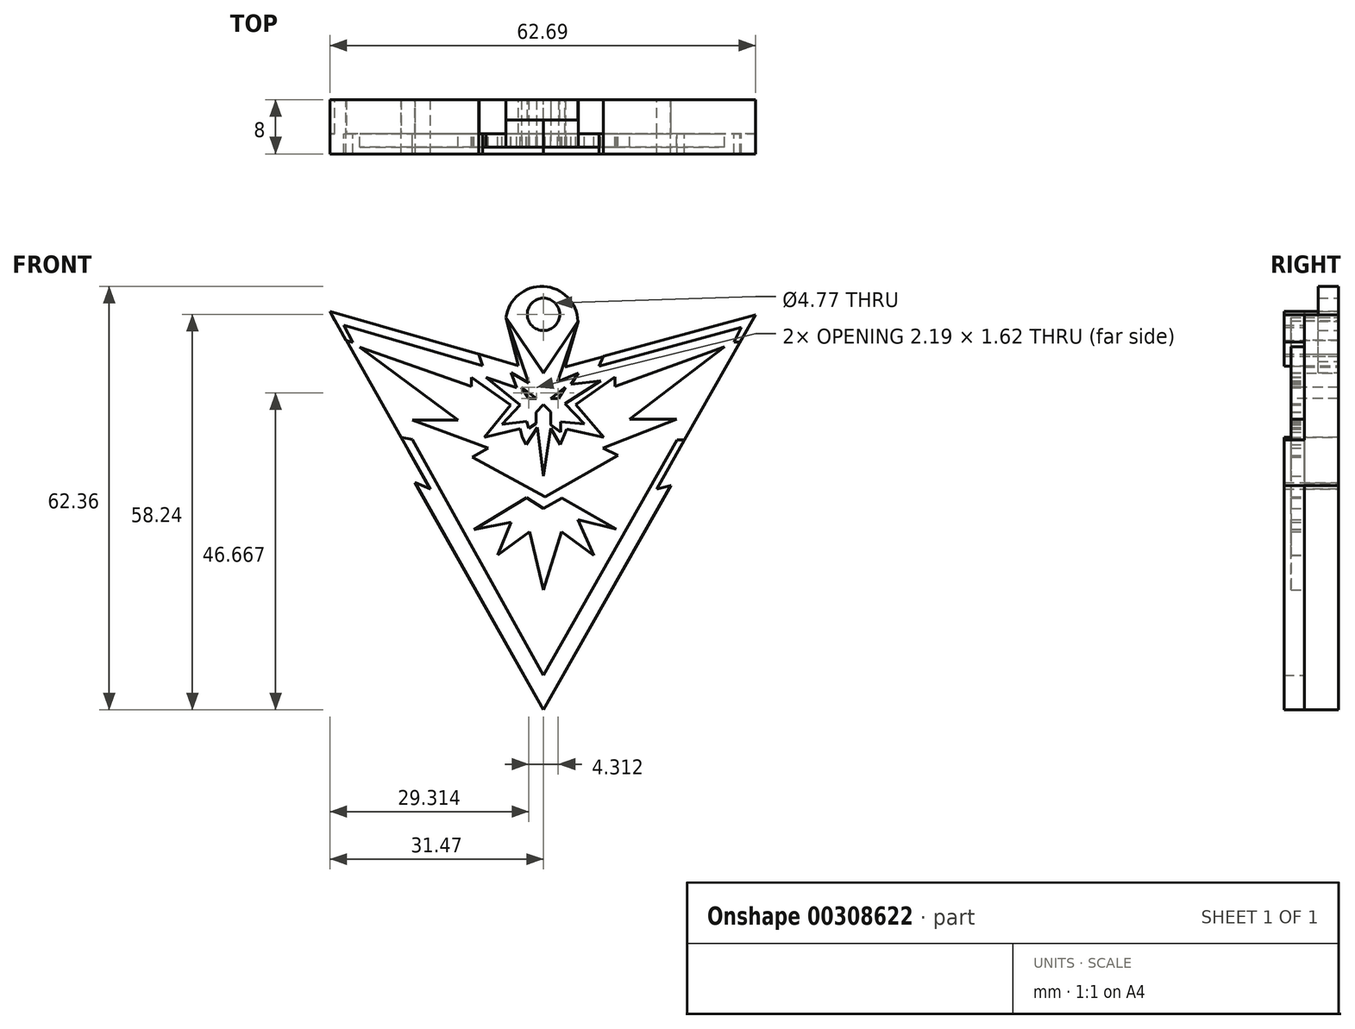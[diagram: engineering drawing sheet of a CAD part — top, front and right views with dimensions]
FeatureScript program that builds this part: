
annotation { "Feature Type Name" : "Feature", "Feature Type Description" : "" }
export const myFeature = defineFeature(function(context is Context, id is Id, definition is map)
    precondition{}
    {
        {
            var Q0;
            Q0=qCreatedBy(makeId("Front.planeOp"),FACE);
            var sketch = newSketch(context, id + "F0", { "sketchPlane" : qUnion([Q0])});
            skLineSegment(sketch, "E0", {"start": v(-31.47, 27.97) * mm, "end": v(-16.64, 1.77) * mm});
            skLineSegment(sketch, "E1", {"start": v(-16.64, 1.77) * mm, "end": v(-18.92, 2.74) * mm});
            skLineSegment(sketch, "E2", {"start": v(-18.92, 2.74) * mm, "end": v(0, -30.7) * mm});
            skLineSegment(sketch, "E3", {"start": v(0, -30.7) * mm, "end": v(18.75, 2.34) * mm});
            skLineSegment(sketch, "E4", {"start": v(18.75, 2.34) * mm, "end": v(16.66, 1.81) * mm});
            skLineSegment(sketch, "E5", {"start": v(16.66, 1.81) * mm, "end": v(31.22, 27.46) * mm});
            skLineSegment(sketch, "E6", {"start": v(31.22, 27.46) * mm, "end": v(3.16, 19.8) * mm});
            skLineSegment(sketch, "E7", {"start": v(-9.51, 21.66) * mm, "end": v(-31.47, 27.97) * mm});
            skPoint(sketch, "E8.start.orphan", {"position": v(0, 17.27) * mm});
            skPoint(sketch, "E9.start.orphan", {"position": v(0, -25.6) * mm});
            skLineSegment(sketch, "E10", {"start": v(-29.08, 23.73) * mm, "end": v(-28.03, 23.44) * mm});
            skLineSegment(sketch, "E11", {"start": v(-28.03, 23.44) * mm, "end": v(-29.42, 25.88) * mm});
            skLineSegment(sketch, "E12", {"start": v(-29.42, 25.88) * mm, "end": v(-8.9, 19.99) * mm});
            skLineSegment(sketch, "E13", {"start": v(-8.9, 19.99) * mm, "end": v(-9.51, 21.66) * mm});
            skLineSegment(sketch, "E14", {"start": v(-20.99, 9.44) * mm, "end": v(-19.31, 9.1) * mm});
            skLineSegment(sketch, "E15", {"start": v(-19.31, 9.1) * mm, "end": v(0, -25.6) * mm});
            skLineSegment(sketch, "E16", {"start": v(0, -25.6) * mm, "end": v(19.67, 9.04) * mm});
            skLineSegment(sketch, "E17", {"start": v(19.67, 9.04) * mm, "end": v(20.77, 9.04) * mm});
            skLineSegment(sketch, "E18", {"start": v(8.86, 21.35) * mm, "end": v(8.22, 19.92) * mm});
            skLineSegment(sketch, "E19", {"start": v(8.22, 19.92) * mm, "end": v(29.1, 25.63) * mm});
            skLineSegment(sketch, "E20", {"start": v(29.1, 25.63) * mm, "end": v(28.09, 23.5) * mm});
            skLineSegment(sketch, "E21", {"start": v(28.09, 23.5) * mm, "end": v(28.97, 23.5) * mm});
            skLineSegment(sketch, "E22", {"start": v(-9.51, 21.66) * mm, "end": v(-3.7, 19.99) * mm});
            skLineSegment(sketch, "E23", {"start": v(-3.7, 19.99) * mm, "end": v(-5.57, 27.1) * mm});
            skLineSegment(sketch, "E24", {"start": v(-5.57, 27.1) * mm, "end": v(0, 18.93) * mm});
            skLineSegment(sketch, "E25", {"start": v(0, 18.93) * mm, "end": v(5.11, 26.6) * mm});
            skLineSegment(sketch, "E26", {"start": v(5.11, 26.6) * mm, "end": v(3.16, 19.8) * mm});
            skSolve(sketch);
        }
        {
            var Q0;
            {var subQ1=sQuery(id+"F0.wireOp",EDGE,"E7");Q0=makeQuery(id+"F0.imprint","IMPRINT",FACE,{"disambiguationData":[TD([[makeQuery(id+"F0.imprint","IMPRINT",EDGE,{"derivedFrom":subQ1}),1.0]])]});}
            var Q1;
            {var subQ1=sQuery(id+"F0.wireOp",EDGE,"E10");Q1=makeQuery(id+"F0.imprint","IMPRINT",FACE,{"disambiguationData":[TD([[makeQuery(id+"F0.imprint","IMPRINT",EDGE,{"derivedFrom":subQ1}),-1.0]])]});}
            var Q2;
            {var subQ0=sQuery(id+"F0.wireOp",EDGE,"E18");Q2=makeQuery(id+"F0.imprint","IMPRINT",FACE,{"disambiguationData":[TD([[makeQuery(id+"F0.imprint","IMPRINT",EDGE,{"derivedFrom":subQ0}),1.0]])]});}
            var Q3;
            {var subQ0=sQuery(id+"F0.wireOp",EDGE,"E1");Q3=makeQuery(id+"F0.imprint","IMPRINT",FACE,{"disambiguationData":[TD([[makeQuery(id+"F0.imprint","IMPRINT",EDGE,{"derivedFrom":subQ0}),1.0]])]});}
            extrude(context, id + "F1", {"entities" : qUnion([Q0, Q1, Q2, Q3]), "depth" : 5 * mm, "offsetDistance" : 25 * mm});
        }
        {
            var Q0;
            Q0=qCreatedBy(makeId("Front.planeOp"),FACE);
            var sketch = newSketch(context, id + "F2", { "sketchPlane" : qUnion([Q0])});
            skLineSegment(sketch, "E27", {"start": v(-31.46, 27.99) * mm, "end": v(-29.13, 23.73) * mm});
            skLineSegment(sketch, "E28", {"start": v(-29.13, 23.73) * mm, "end": v(-28.06, 23.43) * mm});
            skLineSegment(sketch, "E29", {"start": v(-28.06, 23.43) * mm, "end": v(-29.43, 25.93) * mm});
            skLineSegment(sketch, "E30", {"start": v(-29.43, 25.93) * mm, "end": v(-8.95, 20) * mm});
            skLineSegment(sketch, "E31", {"start": v(-8.95, 20) * mm, "end": v(-9.52, 21.7) * mm});
            skLineSegment(sketch, "E32", {"start": v(-9.52, 21.7) * mm, "end": v(-31.46, 27.99) * mm});
            skLineSegment(sketch, "E33", {"start": v(8.82, 21.38) * mm, "end": v(8.17, 19.92) * mm});
            skLineSegment(sketch, "E34", {"start": v(8.17, 19.92) * mm, "end": v(29.15, 25.63) * mm});
            skLineSegment(sketch, "E35", {"start": v(29.15, 25.63) * mm, "end": v(28.06, 23.5) * mm});
            skLineSegment(sketch, "E36", {"start": v(28.06, 23.5) * mm, "end": v(28.95, 23.5) * mm});
            skLineSegment(sketch, "E37", {"start": v(28.95, 23.5) * mm, "end": v(31.2, 27.48) * mm});
            skLineSegment(sketch, "E38", {"start": v(31.2, 27.48) * mm, "end": v(8.82, 21.38) * mm});
            skLineSegment(sketch, "E39", {"start": v(-21, 9.43) * mm, "end": v(-19.32, 9.1) * mm});
            skLineSegment(sketch, "E40", {"start": v(-19.32, 9.1) * mm, "end": v(0, -25.6) * mm});
            skLineSegment(sketch, "E41", {"start": v(0, -25.6) * mm, "end": v(19.66, 9.05) * mm});
            skLineSegment(sketch, "E42", {"start": v(19.66, 9.05) * mm, "end": v(20.77, 9.05) * mm});
            skLineSegment(sketch, "E43", {"start": v(20.77, 9.05) * mm, "end": v(16.68, 1.83) * mm});
            skLineSegment(sketch, "E44", {"start": v(16.68, 1.83) * mm, "end": v(18.74, 2.36) * mm});
            skLineSegment(sketch, "E45", {"start": v(18.74, 2.36) * mm, "end": v(0, -30.67) * mm});
            skLineSegment(sketch, "E46", {"start": v(0, -30.67) * mm, "end": v(-18.9, 2.77) * mm});
            skLineSegment(sketch, "E47", {"start": v(-18.9, 2.77) * mm, "end": v(-16.64, 1.83) * mm});
            skLineSegment(sketch, "E48", {"start": v(-16.64, 1.83) * mm, "end": v(-21, 9.43) * mm});
            skSolve(sketch);
        }
        {
            var Q0;
            Q0 = qSketchRegion(id + "F2", true);
            extrude(context, id + "F3", {"entities" : qUnion([Q0]), "operationType" : NewBodyOperationType.ADD, "depth" : 8 * mm, "offsetDistance" : 25 * mm});
        }
        {
            var Q0;
            {var subQ0=sQuery(id+"F0.wireOp",EDGE,"E6");var subQ1=sQuery(id+"F0.wireOp",EDGE,"E5");var subQ2=sQuery(id+"F0.wireOp",EDGE,"E26");var subQ3=sQuery(id+"F0.wireOp",EDGE,"E25");var subQ4=sQuery(id+"F0.wireOp",EDGE,"E23");var subQ5=sQuery(id+"F0.wireOp",EDGE,"E24");var subQ6=sQuery(id+"F0.wireOp",EDGE,"E0");var subQ7=sQuery(id+"F0.wireOp",EDGE,"E22");var subQ8=sQuery(id+"F0.wireOp",EDGE,"E7");Q0=makeQuery(id+"F3.boolean.opBoolean","SPLIT",FACE,{"disambiguationData":[TD([makeQuery(id+"F1.opExtrude","SWEPT_FACE",FACE,{"disambiguationData":[OSD([subQ1])]})])],"derivedFrom":makeQuery(id+"F1.opExtrude","CAP_FACE",FACE,{"disambiguationData":[OSD([subQ6,sQuery(id+"F0.wireOp",EDGE,"E1"),sQuery(id+"F0.wireOp",EDGE,"E2"),sQuery(id+"F0.wireOp",EDGE,"E3"),sQuery(id+"F0.wireOp",EDGE,"E4"),subQ1,subQ0,subQ8,subQ7,subQ4,subQ5,subQ3,subQ2])],"isStart":false})});}
            var sketch = newSketch(context, id + "F4", { "sketchPlane" : qUnion([Q0])});
            skLineSegment(sketch, "E49", {"start": v(-10.21, -4.18) * mm, "end": v(-2.48, 0.56) * mm});
            skLineSegment(sketch, "E50", {"start": v(-2.48, 0.56) * mm, "end": v(0, -1.04) * mm});
            skLineSegment(sketch, "E51", {"start": v(0, -1.04) * mm, "end": v(2.74, 0.47) * mm});
            skLineSegment(sketch, "E52", {"start": v(2.74, 0.47) * mm, "end": v(10.73, -4.09) * mm});
            skLineSegment(sketch, "E53", {"start": v(10.73, -4.09) * mm, "end": v(5.05, -2.7) * mm});
            skLineSegment(sketch, "E54", {"start": v(5.05, -2.7) * mm, "end": v(7.42, -7.93) * mm});
            skLineSegment(sketch, "E55", {"start": v(7.42, -7.93) * mm, "end": v(2.68, -4.44) * mm});
            skLineSegment(sketch, "E56", {"start": v(2.68, -4.44) * mm, "end": v(0, -13.06) * mm});
            skLineSegment(sketch, "E57", {"start": v(0, -13.06) * mm, "end": v(-2.07, -4.47) * mm});
            skLineSegment(sketch, "E58", {"start": v(-2.07, -4.47) * mm, "end": v(-6.78, -7.87) * mm});
            skLineSegment(sketch, "E59", {"start": v(-6.78, -7.87) * mm, "end": v(-4.8, -3.1) * mm});
            skLineSegment(sketch, "E60", {"start": v(-4.8, -3.1) * mm, "end": v(-10.21, -4.18) * mm});
            skSolve(sketch);
        }
        {
            var Q0;
            Q0 = qSketchRegion(id + "F4", true);
            extrude(context, id + "F5", {"entities" : qUnion([Q0]), "operationType" : NewBodyOperationType.ADD, "depth" : 2 * mm});
        }
        {
            var Q0;
            {var subQ0=sQuery(id+"F0.wireOp",EDGE,"E6");var subQ1=sQuery(id+"F0.wireOp",EDGE,"E5");var subQ2=sQuery(id+"F0.wireOp",EDGE,"E26");var subQ3=sQuery(id+"F0.wireOp",EDGE,"E25");var subQ4=sQuery(id+"F0.wireOp",EDGE,"E23");var subQ5=sQuery(id+"F0.wireOp",EDGE,"E24");var subQ6=sQuery(id+"F0.wireOp",EDGE,"E0");var subQ7=sQuery(id+"F0.wireOp",EDGE,"E22");var subQ8=sQuery(id+"F0.wireOp",EDGE,"E7");Q0=makeQuery(id+"F3.boolean.opBoolean","SPLIT",FACE,{"disambiguationData":[TD([makeQuery(id+"F1.opExtrude","SWEPT_FACE",FACE,{"disambiguationData":[OSD([subQ1])]})])],"derivedFrom":makeQuery(id+"F1.opExtrude","CAP_FACE",FACE,{"disambiguationData":[OSD([subQ6,sQuery(id+"F0.wireOp",EDGE,"E1"),sQuery(id+"F0.wireOp",EDGE,"E2"),sQuery(id+"F0.wireOp",EDGE,"E3"),sQuery(id+"F0.wireOp",EDGE,"E4"),subQ1,subQ0,subQ8,subQ7,subQ4,subQ5,subQ3,subQ2])],"isStart":false})});}
            var sketch = newSketch(context, id + "F6", { "sketchPlane" : qUnion([Q0])});
            skLineSegment(sketch, "E61", {"start": v(-27.04, 22.7) * mm, "end": v(-10.64, 16.92) * mm});
            skLineSegment(sketch, "E62", {"start": v(-10.64, 16.92) * mm, "end": v(-10.64, 18.24) * mm});
            skLineSegment(sketch, "E63", {"start": v(-10.64, 18.24) * mm, "end": v(-4.87, 14.18) * mm});
            skLineSegment(sketch, "E64", {"start": v(-4.87, 14.18) * mm, "end": v(-8.7, 9.43) * mm});
            skLineSegment(sketch, "E65", {"start": v(-8.7, 9.43) * mm, "end": v(-3.44, 10.7) * mm});
            skLineSegment(sketch, "E66", {"start": v(-3.44, 10.7) * mm, "end": v(-3.14, 9.43) * mm});
            skLineSegment(sketch, "E67", {"start": v(-3.14, 9.43) * mm, "end": v(-2.53, 8.35) * mm});
            skLineSegment(sketch, "E68", {"start": v(-2.53, 8.35) * mm, "end": v(-0.93, 10.87) * mm});
            skLineSegment(sketch, "E69", {"start": v(-0.93, 10.87) * mm, "end": v(0, 3.73) * mm});
            skLineSegment(sketch, "E70", {"start": v(0, 3.73) * mm, "end": v(1.07, 10.75) * mm});
            skLineSegment(sketch, "E71", {"start": v(1.07, 10.75) * mm, "end": v(2.44, 8.33) * mm});
            skLineSegment(sketch, "E72", {"start": v(2.44, 8.33) * mm, "end": v(3.41, 10.64) * mm});
            skLineSegment(sketch, "E73", {"start": v(3.41, 10.64) * mm, "end": v(8.9, 9.43) * mm});
            skLineSegment(sketch, "E74", {"start": v(8.9, 9.43) * mm, "end": v(4.73, 14.24) * mm});
            skLineSegment(sketch, "E75", {"start": v(4.73, 14.24) * mm, "end": v(10.55, 18.35) * mm});
            skLineSegment(sketch, "E76", {"start": v(10.55, 18.35) * mm, "end": v(10.55, 16.92) * mm});
            skLineSegment(sketch, "E77", {"start": v(10.55, 16.92) * mm, "end": v(26.67, 22.75) * mm});
            skLineSegment(sketch, "E78", {"start": v(26.67, 22.75) * mm, "end": v(12.67, 12.12) * mm});
            skLineSegment(sketch, "E79", {"start": v(12.67, 12.12) * mm, "end": v(19.58, 12.12) * mm});
            skLineSegment(sketch, "E80", {"start": v(19.58, 12.12) * mm, "end": v(8.73, 7.84) * mm});
            skLineSegment(sketch, "E81", {"start": v(8.73, 7.84) * mm, "end": v(10.95, 6.75) * mm});
            skLineSegment(sketch, "E82", {"start": v(10.95, 6.75) * mm, "end": v(0.24, 0.7) * mm});
            skLineSegment(sketch, "E83", {"start": v(0.24, 0.7) * mm, "end": v(-10.47, 6.53) * mm});
            skLineSegment(sketch, "E84", {"start": v(-10.47, 6.53) * mm, "end": v(-8.15, 7.84) * mm});
            skLineSegment(sketch, "E85", {"start": v(-8.15, 7.84) * mm, "end": v(-19.33, 11.95) * mm});
            skLineSegment(sketch, "E86", {"start": v(-19.33, 11.95) * mm, "end": v(-12.59, 11.95) * mm});
            skLineSegment(sketch, "E87", {"start": v(-12.59, 11.95) * mm, "end": v(-27.04, 22.7) * mm});
            skSolve(sketch);
        }
        {
            var Q0;
            Q0 = qSketchRegion(id + "F6", true);
            extrude(context, id + "F7", {"entities" : qUnion([Q0]), "operationType" : NewBodyOperationType.ADD, "depth" : 2 * mm});
        }
        {
            var Q0;
            {var subQ0=sQuery(id+"F0.wireOp",EDGE,"E6");var subQ1=sQuery(id+"F0.wireOp",EDGE,"E5");var subQ2=sQuery(id+"F0.wireOp",EDGE,"E26");var subQ3=sQuery(id+"F0.wireOp",EDGE,"E25");var subQ4=sQuery(id+"F0.wireOp",EDGE,"E23");var subQ5=sQuery(id+"F0.wireOp",EDGE,"E24");var subQ6=sQuery(id+"F0.wireOp",EDGE,"E0");var subQ7=sQuery(id+"F0.wireOp",EDGE,"E22");var subQ8=sQuery(id+"F0.wireOp",EDGE,"E7");Q0=makeQuery(id+"F3.boolean.opBoolean","SPLIT",FACE,{"disambiguationData":[TD([makeQuery(id+"F1.opExtrude","SWEPT_FACE",FACE,{"disambiguationData":[OSD([subQ1])]})])],"derivedFrom":makeQuery(id+"F1.opExtrude","CAP_FACE",FACE,{"disambiguationData":[OSD([subQ6,sQuery(id+"F0.wireOp",EDGE,"E1"),sQuery(id+"F0.wireOp",EDGE,"E2"),sQuery(id+"F0.wireOp",EDGE,"E3"),sQuery(id+"F0.wireOp",EDGE,"E4"),subQ1,subQ0,subQ8,subQ7,subQ4,subQ5,subQ3,subQ2])],"isStart":false})});}
            var sketch = newSketch(context, id + "F8", { "sketchPlane" : qUnion([Q0])});
            skLineSegment(sketch, "E88", {"start": v(-6.12, 11.34) * mm, "end": v(-3.42, 14.18) * mm});
            skLineSegment(sketch, "E89", {"start": v(-3.42, 14.18) * mm, "end": v(-8.46, 18.25) * mm});
            skLineSegment(sketch, "E90", {"start": v(-8.46, 18.25) * mm, "end": v(-3.96, 16.74) * mm});
            skLineSegment(sketch, "E91", {"start": v(-3.96, 16.74) * mm, "end": v(-4.79, 18.94) * mm});
            skLineSegment(sketch, "E92", {"start": v(-4.79, 18.94) * mm, "end": v(-2.2, 17.46) * mm});
            skLineSegment(sketch, "E93", {"start": v(-2.2, 17.46) * mm, "end": v(-5.57, 27.1) * mm});
            skLineSegment(sketch, "E94", {"start": v(-5.57, 27.1) * mm, "end": v(0, 18.93) * mm});
            skLineSegment(sketch, "E95", {"start": v(0, 18.93) * mm, "end": v(5.11, 26.6) * mm});
            skLineSegment(sketch, "E96", {"start": v(5.11, 26.6) * mm, "end": v(2.08, 17.64) * mm});
            skLineSegment(sketch, "E97", {"start": v(2.08, 17.64) * mm, "end": v(5.11, 18.93) * mm});
            skLineSegment(sketch, "E98", {"start": v(5.11, 18.93) * mm, "end": v(4.06, 17.24) * mm});
            skLineSegment(sketch, "E99", {"start": v(4.06, 17.24) * mm, "end": v(8.42, 17.75) * mm});
            skLineSegment(sketch, "E100", {"start": v(8.42, 17.75) * mm, "end": v(3.16, 14.36) * mm});
            skLineSegment(sketch, "E101", {"start": v(3.16, 14.36) * mm, "end": v(6, 11.41) * mm});
            skLineSegment(sketch, "E102", {"start": v(6, 11.41) * mm, "end": v(2.52, 11.7) * mm});
            skLineSegment(sketch, "E103", {"start": v(2.52, 11.7) * mm, "end": v(2.52, 10.23) * mm});
            skLineSegment(sketch, "E104", {"start": v(2.52, 10.23) * mm, "end": v(1.07, 11.27) * mm});
            skLineSegment(sketch, "E105", {"start": v(1.07, 11.27) * mm, "end": v(1.07, 13.18) * mm});
            skLineSegment(sketch, "E106", {"start": v(1.07, 13.18) * mm, "end": v(0, 14.24) * mm});
            skLineSegment(sketch, "E107", {"start": v(0, 14.24) * mm, "end": v(-1.09, 13.14) * mm});
            skLineSegment(sketch, "E108", {"start": v(-1.09, 13.14) * mm, "end": v(-1.09, 11.49) * mm});
            skLineSegment(sketch, "E109", {"start": v(-1.09, 11.49) * mm, "end": v(-2.2, 10.75) * mm});
            skLineSegment(sketch, "E110", {"start": v(-2.2, 10.75) * mm, "end": v(-2.52, 11.8) * mm});
            skLineSegment(sketch, "E111", {"start": v(-2.52, 11.8) * mm, "end": v(-6.12, 11.34) * mm});
            skSolve(sketch);
        }
        {
            var Q0;
            Q0 = qSketchRegion(id + "F8", true);
            extrude(context, id + "F9", {"entities" : qUnion([Q0]), "operationType" : NewBodyOperationType.ADD, "depth" : 2 * mm});
        }
        {
            var Q0;
            Q0=qCreatedBy(makeId("Front.planeOp"),FACE);
            var sketch = newSketch(context, id + "F10", { "sketchPlane" : qUnion([Q0])});
            skLineSegment(sketch, "E112", {"start": v(0, 18.97) * mm, "end": v(2.04, 21.96) * mm});
            skLineSegment(sketch, "E113", {"start": v(0, 18.97) * mm, "end": v(-5.54, 27.07) * mm});
            skLineSegment(sketch, "E114", {"start": v(2.04, 21.96) * mm, "end": v(5.06, 26.5) * mm});
            skArc(sketch, "E115", {"start": v(5.06, 26.5) * mm, "mid": v(0.02, 31.66) * mm, "end": v(-5.54, 27.07) * mm});
            skCircle(sketch, "E116", {"center": v(0, 27.55) * mm, "radius": 2.39 * mm});
            skSolve(sketch);
        }
        {
            var Q0;
            Q0 = qSketchRegion(id + "F10", true);
            extrude(context, id + "F11", {"entities" : qUnion([Q0]), "operationType" : NewBodyOperationType.ADD, "depth" : 3 * mm});
        }
        {
            var Q0;
            Q0=makeQuery(id+"F9.opExtrude","CAP_FACE",FACE,{"disambiguationData":[OSD([sQuery(id+"F8.wireOp",EDGE,"E88"),sQuery(id+"F8.wireOp",EDGE,"E89"),sQuery(id+"F8.wireOp",EDGE,"E90"),sQuery(id+"F8.wireOp",EDGE,"E91"),sQuery(id+"F8.wireOp",EDGE,"E92"),sQuery(id+"F8.wireOp",EDGE,"E93"),sQuery(id+"F8.wireOp",EDGE,"E94"),sQuery(id+"F8.wireOp",EDGE,"E95"),sQuery(id+"F8.wireOp",EDGE,"E96"),sQuery(id+"F8.wireOp",EDGE,"E97"),sQuery(id+"F8.wireOp",EDGE,"E98"),sQuery(id+"F8.wireOp",EDGE,"E99"),sQuery(id+"F8.wireOp",EDGE,"E100"),sQuery(id+"F8.wireOp",EDGE,"E101"),sQuery(id+"F8.wireOp",EDGE,"E102"),sQuery(id+"F8.wireOp",EDGE,"E103"),sQuery(id+"F8.wireOp",EDGE,"E104"),sQuery(id+"F8.wireOp",EDGE,"E105"),sQuery(id+"F8.wireOp",EDGE,"E106"),sQuery(id+"F8.wireOp",EDGE,"E107"),sQuery(id+"F8.wireOp",EDGE,"E108"),sQuery(id+"F8.wireOp",EDGE,"E109"),sQuery(id+"F8.wireOp",EDGE,"E110"),sQuery(id+"F8.wireOp",EDGE,"E111")])],"isStart":false});
            var sketch = newSketch(context, id + "F12", { "sketchPlane" : qUnion([Q0])});
            skLineSegment(sketch, "E117", {"start": v(1.06, 15.17) * mm, "end": v(2.2, 15.17) * mm});
            skLineSegment(sketch, "E118", {"start": v(2.2, 15.17) * mm, "end": v(3.25, 16.79) * mm});
            skLineSegment(sketch, "E119", {"start": v(3.25, 16.79) * mm, "end": v(1.06, 15.17) * mm});
            skLineSegment(sketch, "E120.MirrorCS", {"start": v(-3.25, 16.79) * mm, "end": v(-1.06, 15.17) * mm});
            skLineSegment(sketch, "E121.MirrorCS", {"start": v(-1.06, 15.17) * mm, "end": v(-2.2, 15.17) * mm});
            skLineSegment(sketch, "E122.MirrorCS", {"start": v(-2.2, 15.17) * mm, "end": v(-3.25, 16.79) * mm});
            skSolve(sketch);
        }
        {
            var Q0;
            Q0 = qSketchRegion(id + "F12", true);
            extrude(context, id + "F13", {"entities" : qUnion([Q0]), "operationType" : NewBodyOperationType.REMOVE, "oppositeDirection" : true, "depth" : 8 * mm});
        }
    });
